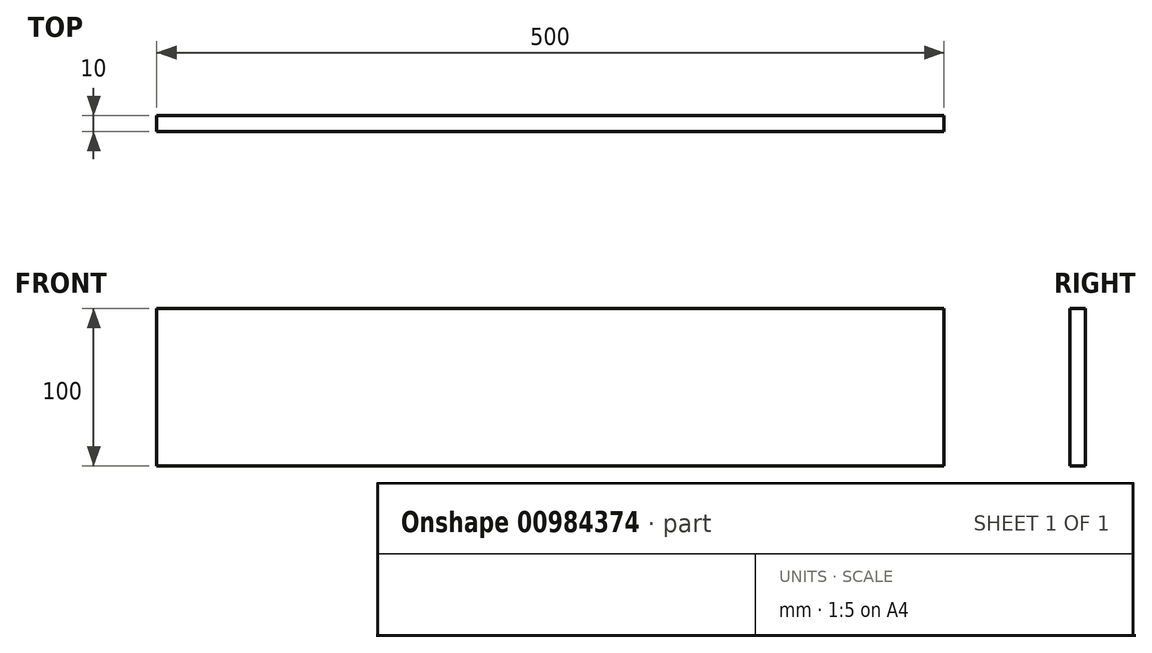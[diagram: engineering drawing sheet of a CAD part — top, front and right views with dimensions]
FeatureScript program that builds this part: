
annotation { "Feature Type Name" : "Feature", "Feature Type Description" : "" }
export const myFeature = defineFeature(function(context is Context, id is Id, definition is map)
    precondition{}
    {
        {
            var Q0;
            Q0=qCreatedBy(makeId("Front.planeOp"),FACE);
            var sketch = newSketch(context, id + "F0", { "sketchPlane" : qUnion([Q0])});
            skLineSegment(sketch, "E0.bottom", {"start": v(250, -50) * mm, "end": v(-250, -50) * mm});
            skLineSegment(sketch, "E0.top", {"start": v(250, 50) * mm, "end": v(-250, 50) * mm});
            skLineSegment(sketch, "E0.left", {"start": v(250, -50) * mm, "end": v(250, 50) * mm});
            skLineSegment(sketch, "E0.right", {"start": v(-250, -50) * mm, "end": v(-250, 50) * mm});
            skPoint(sketch, "E0.middle", {"position": v(0, 0) * mm});
            skSolve(sketch);
        }
        {
            var Q0;
            Q0=qSketchRegion(id+"F0",true);
            extrude(context, id + "F1", {"entities" : qUnion([Q0]), "oppositeDirection" : true, "depth" : 10 * mm, "offsetDistance" : 25 * mm});
        }
    });
